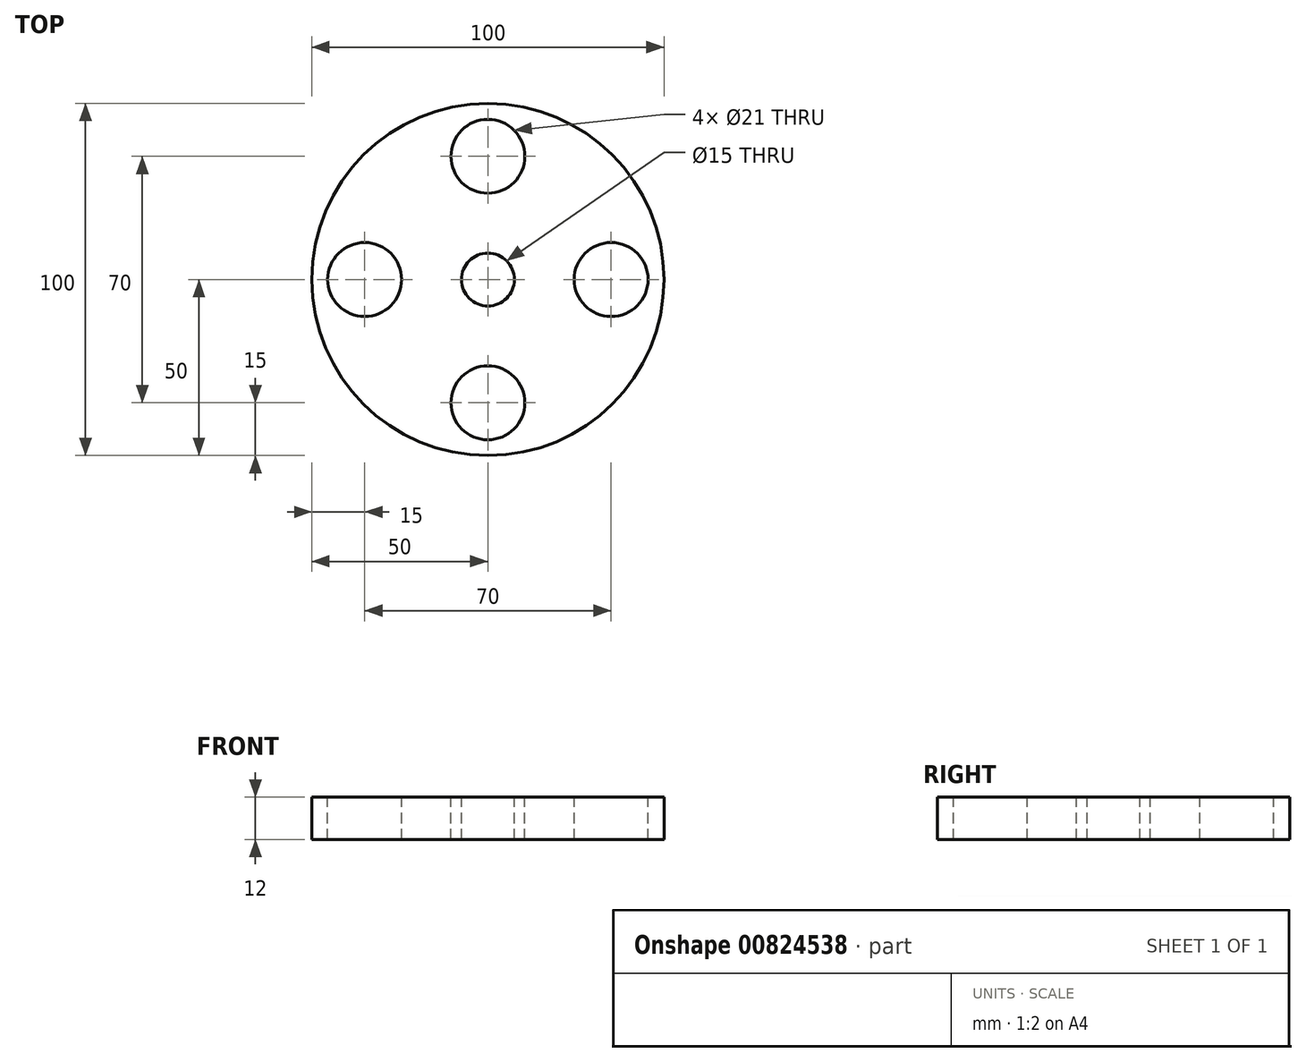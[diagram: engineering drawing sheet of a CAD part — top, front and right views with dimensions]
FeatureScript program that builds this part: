
annotation { "Feature Type Name" : "Feature", "Feature Type Description" : "" }
export const myFeature = defineFeature(function(context is Context, id is Id, definition is map)
    precondition{}
    {
        {
            var Q0;
            Q0=qCreatedBy(makeId("Top.planeOp"),FACE);
            var sketch = newSketch(context, id + "F0", { "sketchPlane" : qUnion([Q0])});
            skCircle(sketch, "E0", {"center": v(0, 0) * mm, "radius": 50 * mm});
            skCircle(sketch, "E1", {"center": v(35, 0) * mm, "radius": 10.5 * mm});
            skCircle(sketch, "E2", {"center": v(0, 35) * mm, "radius": 10.5 * mm});
            skCircle(sketch, "E3", {"center": v(-35, 0) * mm, "radius": 10.5 * mm});
            skCircle(sketch, "E4", {"center": v(0, -35) * mm, "radius": 10.5 * mm});
            skCircle(sketch, "E5", {"center": v(0, 0) * mm, "radius": 7.5 * mm});
            skSolve(sketch);
        }
        {
            var Q0;
            Q0=makeQuery(id+"F0.imprint","IMPRINT",FACE,{"disambiguationData":[TD([[makeQuery(id+"F0.imprint","IMPRINT",EDGE,{"derivedFrom":sQuery(id+"F0.wireOp",EDGE,"E0")}),1.0]])]});
            extrude(context, id + "F1", {"entities" : qUnion([Q0]), "oppositeDirection" : true, "depth" : 10 * mm});
        }
        {
            var Q0;
            Q0=makeQuery(id+"F0.imprint","IMPRINT",FACE,{"disambiguationData":[TD([[makeQuery(id+"F0.imprint","IMPRINT",EDGE,{"derivedFrom":sQuery(id+"F0.wireOp",EDGE,"E0")}),1.0]])]});
            extrude(context, id + "F2", {"entities" : qUnion([Q0]), "operationType" : NewBodyOperationType.ADD, "depth" : 2 * mm});
        }
    });
